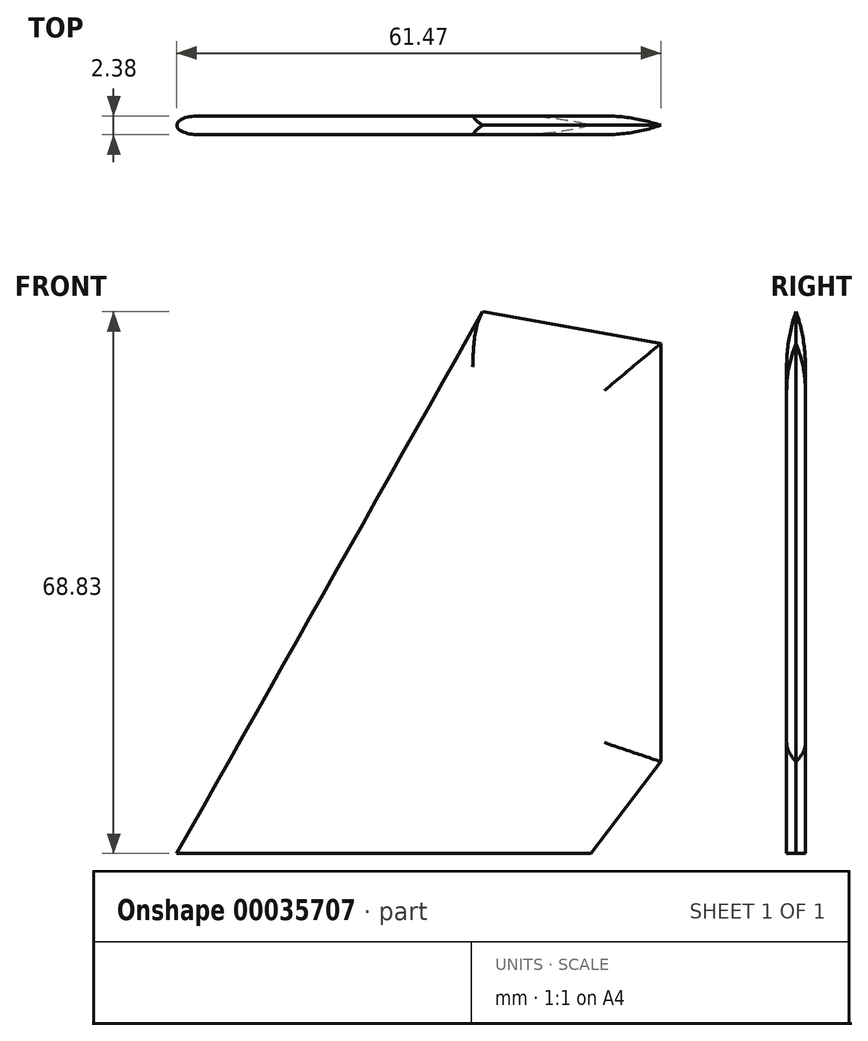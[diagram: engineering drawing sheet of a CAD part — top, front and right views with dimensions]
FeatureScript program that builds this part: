
annotation { "Feature Type Name" : "Feature", "Feature Type Description" : "" }
export const myFeature = defineFeature(function(context is Context, id is Id, definition is map)
    precondition{}
    {
        {
            var Q0;
            Q0=qCreatedBy(makeId("Front.planeOp"),FACE);
            var sketch = newSketch(context, id + "F0", { "sketchPlane" : qUnion([Q0])});
            skLineSegment(sketch, "E0", {"start": v(0, 0) * mm, "end": v(43.69, 77.47) * mm});
            skLineSegment(sketch, "E1", {"start": v(59.18, 0) * mm, "end": v(0, 0) * mm});
            skLineSegment(sketch, "E2", {"start": v(68.07, 11.68) * mm, "end": v(6.59, 11.68) * mm, "construction": true});
            skLineSegment(sketch, "E3", {"start": v(56.13, 57.67) * mm, "end": v(56.13, 11.68) * mm});
            skLineSegment(sketch, "E4", {"start": v(68.07, 73.15) * mm, "end": v(68.07, 11.68) * mm});
            skLineSegment(sketch, "E5", {"start": v(43.69, 77.47) * mm, "end": v(68.07, 73.15) * mm});
            skLineSegment(sketch, "E6", {"start": v(34.66, 61.47) * mm, "end": v(56.13, 57.67) * mm});
            skLineSegment(sketch, "E7", {"start": v(38.82, 68.83) * mm, "end": v(61.47, 64.82) * mm});
            skLineSegment(sketch, "E8", {"start": v(61.47, 64.82) * mm, "end": v(61.47, 11.68) * mm});
            skLineSegment(sketch, "E9", {"start": v(56.13, 11.68) * mm, "end": v(47.24, 0) * mm});
            skLineSegment(sketch, "E10", {"start": v(61.47, 11.68) * mm, "end": v(52.58, 0) * mm});
            skLineSegment(sketch, "E11", {"start": v(68.07, 11.68) * mm, "end": v(59.18, 0) * mm});
            skSolve(sketch);
        }
        {
            var Q0;
            Q0=makeQuery(id+"F0.imprint","IMPRINT",FACE,{"disambiguationData":[TD([[makeQuery(id+"F0.imprint","IMPRINT",EDGE,{"derivedFrom":sQuery(id+"F0.wireOp",EDGE,"E3")}),-1.0]])]});
            var Q1;
            Q1=makeQuery(id+"F0.imprint","IMPRINT",FACE,{"disambiguationData":[TD([[makeQuery(id+"F0.imprint","IMPRINT",EDGE,{"derivedFrom":sQuery(id+"F0.wireOp",EDGE,"E3")}),1.0]])]});
            extrude(context, id + "F1", {"entities" : qUnion([Q0, Q1]), "depth" : 2.38 * mm, "symmetric" : true});
        }
        {
            var Q0;
            Q0=sQuery(id+"F0.wireOp",EDGE,"E0");
            var Q1;
            Q1=sQuery(id+"F0.wireOp",VERTEX,"E0.start");
            cPlane(context, id + "F2", {"entities" : qUnion([Q0, Q1]), "cplaneType" : CPlaneType.LINE_POINT, "offset" : 152.4 * mm, "width" : 152.4 * mm, "height" : 152.4 * mm});
        }
        {
            var Q0;
            Q0=qCreatedBy(id+"F2.planeOp",FACE);
            var sketch = newSketch(context, id + "F3", { "sketchPlane" : qUnion([Q0])});
            skLineSegment(sketch, "E12.0", {"start": v(0, -1.2) * mm, "end": v(21.7, -1.2) * mm});
            skLineSegment(sketch, "E13.1", {"start": v(0, 1.2) * mm, "end": v(21.7, 1.2) * mm});
            skLineSegment(sketch, "E14.0", {"start": v(0, -1.2) * mm, "end": v(21.7, -1.2) * mm, "construction": true});
            skLineSegment(sketch, "E14.1", {"start": v(0, 1.2) * mm, "end": v(21.7, 1.2) * mm, "construction": true});
            skLineSegment(sketch, "E14.2", {"start": v(0, -1.2) * mm, "end": v(0, 1.2) * mm, "construction": true});
            skLineSegment(sketch, "E15", {"start": v(2.38, 1.2) * mm, "end": v(2.38, -1.2) * mm});
            skLineSegment(sketch, "E16", {"start": v(2.38, -1.2) * mm, "end": v(2.38, -3.73) * mm});
            skLineSegment(sketch, "E17", {"start": v(2.38, -3.73) * mm, "end": v(-2.54, -3.73) * mm});
            skLineSegment(sketch, "E18", {"start": v(-2.54, -3.73) * mm, "end": v(-2.54, 0) * mm});
            skLineSegment(sketch, "E19", {"start": v(0, 0) * mm, "end": v(2.38, 0) * mm});
            skLineSegment(sketch, "E20", {"start": v(2.38, 0) * mm, "end": v(0, 0) * mm});
            skEllipticalArc(sketch, "E21", {});
            skLineSegment(sketch, "E22.MirrorCS", {"start": v(2.38, 1.2) * mm, "end": v(2.38, 3.73) * mm});
            skLineSegment(sketch, "E23.MirrorCS", {"start": v(2.38, 3.73) * mm, "end": v(-2.54, 3.73) * mm});
            skLineSegment(sketch, "E24.MirrorCS", {"start": v(-2.54, 3.73) * mm, "end": v(-2.54, 0) * mm});
            const initialGuessF3  = {"E21": [0.00238125, 0, -1, 0, 0.00238125, 0.001190625, 4.71238898038469, 1.5707963267948966]};
            skSetInitialGuess(sketch, initialGuessF3);
            skSolve(sketch);
        }
        {
            var Q0;
            {var subQ4=sQuery(id+"F3.wireOp",EDGE,"E16");Q0=makeQuery(id+"F3.imprint","IMPRINT",FACE,{"disambiguationData":[TD([[makeQuery(id+"F3.imprint","IMPRINT",EDGE,{"derivedFrom":subQ4}),-1.0]])]});}
            extrude(context, id + "F4", {"entities" : qUnion([Q0]), "operationType" : NewBodyOperationType.REMOVE, "endBound" : BoundingType.THROUGH_ALL, "depth" : 25.4 * mm});
        }
        {
            var Q0;
            Q0=sQuery(id+"F0.wireOp",EDGE,"E10");
            var Q1;
            Q1=sQuery(id+"F0.wireOp",VERTEX,"E10.end");
            cPlane(context, id + "F5", {"entities" : qUnion([Q0, Q1]), "cplaneType" : CPlaneType.LINE_POINT, "offset" : 152.4 * mm, "width" : 152.4 * mm, "height" : 152.4 * mm});
        }
        {
            var Q0;
            Q0=qCreatedBy(id+"F5.planeOp",FACE);
            var sketch = newSketch(context, id + "F6", { "sketchPlane" : qUnion([Q0])});
            skLineSegment(sketch, "E25.0", {"start": v(41.84, -1.2) * mm, "end": v(2.18, -1.2) * mm, "construction": true});
            skLineSegment(sketch, "E26.0", {"start": v(41.84, -1.2) * mm, "end": v(2.18, -1.2) * mm});
            skLineSegment(sketch, "E26.1", {"start": v(41.84, 1.2) * mm, "end": v(2.18, 1.2) * mm});
            skLineSegment(sketch, "E27.1", {"start": v(41.84, 1.2) * mm, "end": v(2.18, 1.2) * mm, "construction": true});
            skLineSegment(sketch, "E27.2", {"start": v(41.84, 1.2) * mm, "end": v(41.84, -1.2) * mm, "construction": true});
            skLineSegment(sketch, "E28", {"start": v(34.7, -1.2) * mm, "end": v(34.7, 1.2) * mm});
            skLineSegment(sketch, "E29", {"start": v(34.7, 1.2) * mm, "end": v(34.7, 3.73) * mm});
            skLineSegment(sketch, "E30", {"start": v(34.7, 3.73) * mm, "end": v(44.38, 3.73) * mm});
            skLineSegment(sketch, "E31", {"start": v(44.38, 3.73) * mm, "end": v(44.38, 0) * mm});
            skArc(sketch, "E32", {"start": v(41.84, 0) * mm, "mid": v(38.32, 0.9) * mm, "end": v(34.7, 1.2) * mm});
            skPoint(sketch, "E32.endSnap0", {"position": v(41.84, 0) * mm});
            skPoint(sketch, "E33.orphan", {"position": v(27.56, 0) * mm});
            skArc(sketch, "E34.MirrorCS", {"start": v(41.84, 0) * mm, "mid": v(38.32, -0.9) * mm, "end": v(34.7, -1.2) * mm});
            skLineSegment(sketch, "E35.MirrorCS", {"start": v(44.38, -3.73) * mm, "end": v(44.38, 0) * mm});
            skLineSegment(sketch, "E36.MirrorCS", {"start": v(34.7, -3.73) * mm, "end": v(44.38, -3.73) * mm});
            skLineSegment(sketch, "E37.MirrorCS", {"start": v(34.7, -1.2) * mm, "end": v(34.7, -3.73) * mm});
            skSolve(sketch);
        }
        {
            var Q0;
            Q0=makeQuery(id+"F6.imprint","IMPRINT",FACE,{"disambiguationData":[TD([[makeQuery(id+"F6.imprint","IMPRINT",EDGE,{"derivedFrom":sQuery(id+"F6.wireOp",EDGE,"E29")}),-1.0]])]});
            extrude(context, id + "F7", {"entities" : qUnion([Q0]), "operationType" : NewBodyOperationType.REMOVE, "oppositeDirection" : true, "depth" : 76.2 * mm, "symmetric" : true});
        }
        {
            var Q0;
            Q0=qCreatedBy(makeId("Top.planeOp"),FACE);
            var sketch = newSketch(context, id + "F8", { "sketchPlane" : qUnion([Q0])});
            skLineSegment(sketch, "E38.0", {"start": v(41.3, 1.2) * mm, "end": v(61.47, 1.2) * mm, "construction": true});
            skLineSegment(sketch, "E39.1", {"start": v(41.3, -1.2) * mm, "end": v(61.47, -1.2) * mm, "construction": true});
            skLineSegment(sketch, "E40.2", {"start": v(61.47, -1.2) * mm, "end": v(61.47, 1.2) * mm, "construction": true});
            skLineSegment(sketch, "E41", {"start": v(54.32, -1.2) * mm, "end": v(54.32, 1.2) * mm});
            skLineSegment(sketch, "E42", {"start": v(54.32, 1.2) * mm, "end": v(54.32, 3.73) * mm});
            skLineSegment(sketch, "E43", {"start": v(54.32, 3.73) * mm, "end": v(64, 3.73) * mm});
            skLineSegment(sketch, "E44", {"start": v(64, 3.73) * mm, "end": v(64, 0) * mm});
            skArc(sketch, "E45", {"start": v(61.47, 0) * mm, "mid": v(57.95, 0.9) * mm, "end": v(54.32, 1.2) * mm});
            skPoint(sketch, "E45.endSnap0", {"position": v(61.47, 0) * mm});
            skPoint(sketch, "E46.orphan", {"position": v(47.18, 0) * mm});
            skLineSegment(sketch, "E47.MirrorCS", {"start": v(54.32, -1.2) * mm, "end": v(54.32, -3.73) * mm});
            skLineSegment(sketch, "E48.MirrorCS", {"start": v(54.32, -3.73) * mm, "end": v(64, -3.73) * mm});
            skLineSegment(sketch, "E49.MirrorCS", {"start": v(64, -3.73) * mm, "end": v(64, 0) * mm});
            skArc(sketch, "E50.MirrorCS", {"start": v(61.47, 0) * mm, "mid": v(57.95, -0.9) * mm, "end": v(54.32, -1.2) * mm});
            skSolve(sketch);
        }
        {
            var Q0;
            Q0=makeQuery(id+"F8.imprint","IMPRINT",FACE,{"disambiguationData":[TD([[makeQuery(id+"F8.imprint","IMPRINT",EDGE,{"derivedFrom":sQuery(id+"F8.wireOp",EDGE,"E42")}),-1.0]])]});
            extrude(context, id + "F9", {"entities" : qUnion([Q0]), "operationType" : NewBodyOperationType.REMOVE, "endBound" : BoundingType.THROUGH_ALL, "depth" : 25.4 * mm});
        }
        {
            var Q0;
            Q0=sQuery(id+"F0.wireOp",EDGE,"E7");
            var Q1;
            Q1=sQuery(id+"F0.wireOp",VERTEX,"E7.end");
            cPlane(context, id + "F10", {"entities" : qUnion([Q0, Q1]), "cplaneType" : CPlaneType.LINE_POINT, "offset" : 152.4 * mm, "width" : 152.4 * mm, "height" : 152.4 * mm});
        }
        {
            var Q0;
            Q0=qCreatedBy(id+"F10.planeOp",FACE);
            var sketch = newSketch(context, id + "F11", { "sketchPlane" : qUnion([Q0])});
            skLineSegment(sketch, "E51.0", {"start": v(1.2, 74.55) * mm, "end": v(1.2, 0.48) * mm, "construction": true});
            skLineSegment(sketch, "E52.1", {"start": v(-1.2, 74.55) * mm, "end": v(-1.2, 0.48) * mm, "construction": true});
            skFitSpline(sketch, "E53.2", {"points": [v(-1.2, 74.55) * mm, v(-0.4, 74.55) * mm, v(0.4, 74.55) * mm, v(1.2, 74.55) * mm], "construction": true});
            skLineSegment(sketch, "E54", {"start": v(-1.2, 67.4) * mm, "end": v(1.2, 67.4) * mm});
            skLineSegment(sketch, "E55", {"start": v(1.2, 67.4) * mm, "end": v(3.73, 67.4) * mm});
            skLineSegment(sketch, "E56", {"start": v(3.73, 67.4) * mm, "end": v(3.73, 77.09) * mm});
            skLineSegment(sketch, "E57", {"start": v(3.73, 77.09) * mm, "end": v(0, 77.09) * mm});
            skArc(sketch, "E58", {"start": v(1.2, 67.4) * mm, "mid": v(0.9, 71.03) * mm, "end": v(0, 74.55) * mm});
            skPoint(sketch, "E59.orphan", {"position": v(0, 60.26) * mm});
            skLineSegment(sketch, "E60.MirrorCS", {"start": v(-3.73, 77.09) * mm, "end": v(0, 77.09) * mm});
            skLineSegment(sketch, "E61.MirrorCS", {"start": v(-3.73, 67.4) * mm, "end": v(-3.73, 77.09) * mm});
            skLineSegment(sketch, "E62.MirrorCS", {"start": v(-1.2, 67.4) * mm, "end": v(-3.73, 67.4) * mm});
            skArc(sketch, "E63.MirrorCS", {"start": v(-1.2, 67.4) * mm, "mid": v(-0.9, 71.03) * mm, "end": v(0, 74.55) * mm});
            skSolve(sketch);
        }
        {
            var Q0;
            Q0=makeQuery(id+"F11.imprint","IMPRINT",FACE,{"disambiguationData":[TD([[makeQuery(id+"F11.imprint","IMPRINT",EDGE,{"derivedFrom":sQuery(id+"F11.wireOp",EDGE,"E55")}),1.0]])]});
            extrude(context, id + "F12", {"entities" : qUnion([Q0]), "operationType" : NewBodyOperationType.REMOVE, "oppositeDirection" : true, "depth" : 76.2 * mm, "symmetric" : true});
        }
    });
